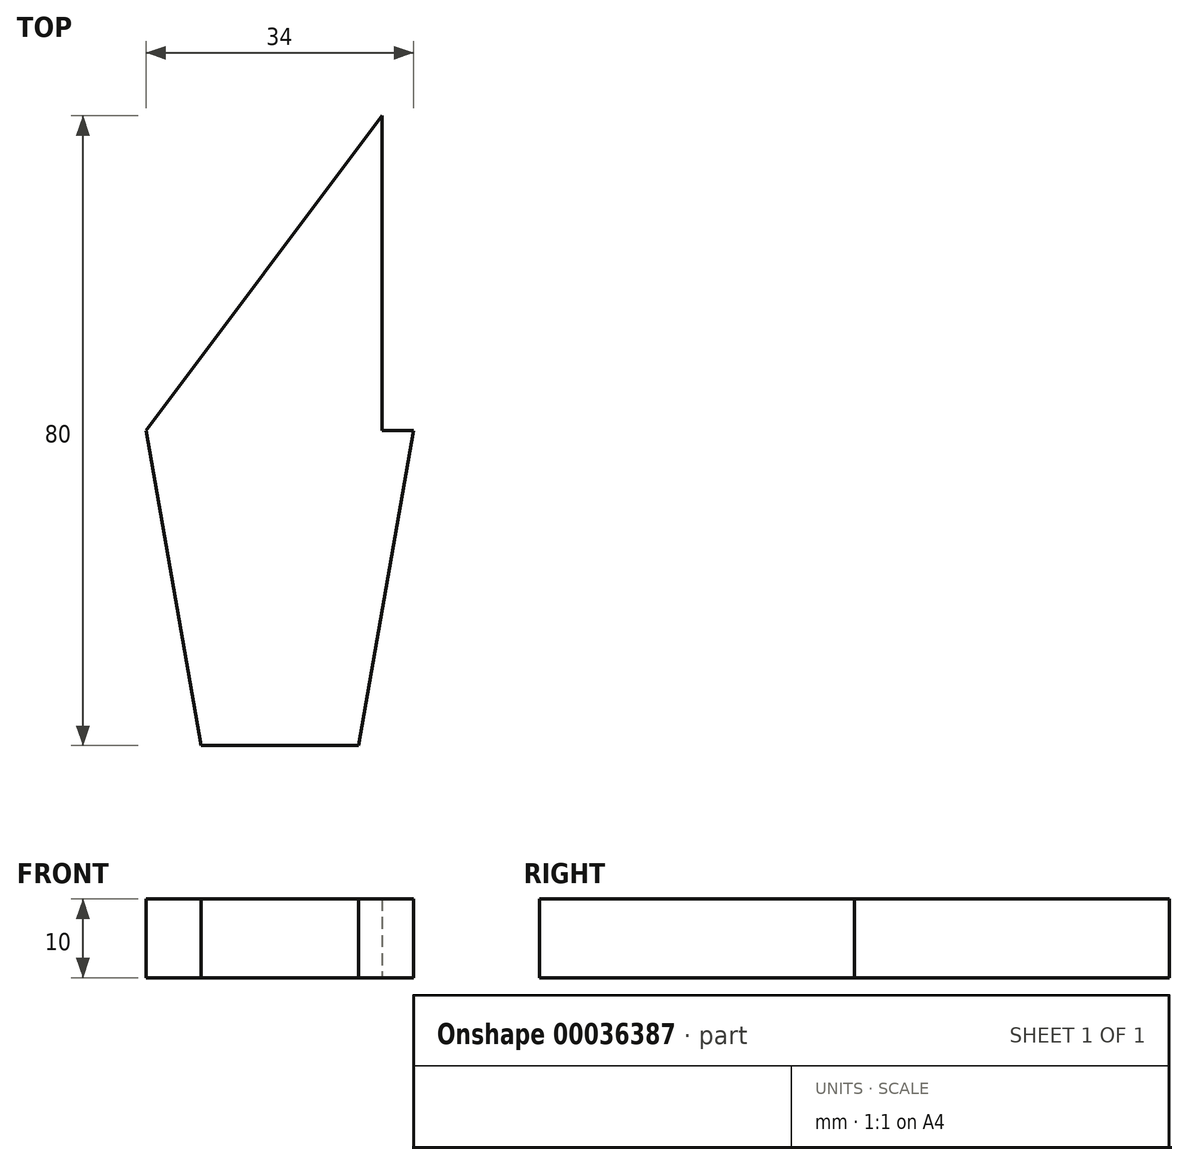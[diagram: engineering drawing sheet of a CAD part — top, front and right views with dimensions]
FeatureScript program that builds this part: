
annotation { "Feature Type Name" : "Feature", "Feature Type Description" : "" }
export const myFeature = defineFeature(function(context is Context, id is Id, definition is map)
    precondition{}
    {
        {
            var Q0;
            Q0=qCreatedBy(makeId("Top.planeOp"),FACE);
            var sketch = newSketch(context, id + "F0", { "sketchPlane" : qUnion([Q0])});
            skLineSegment(sketch, "E0.bottom", {"start": v(-54.45, 18.14) * mm, "end": v(-20.45, 18.14) * mm});
            skLineSegment(sketch, "E0.top", {"start": v(-47.45, -21.86) * mm, "end": v(-27.45, -21.86) * mm});
            skLineSegment(sketch, "E1", {"start": v(-54.45, 18.14) * mm, "end": v(-47.45, -21.86) * mm});
            skLineSegment(sketch, "E2", {"start": v(-20.45, 18.14) * mm, "end": v(-27.45, -21.86) * mm});
            skLineSegment(sketch, "E3", {"start": v(-24.45, 18.14) * mm, "end": v(-24.45, 58.14) * mm});
            skLineSegment(sketch, "E4", {"start": v(-24.45, 58.14) * mm, "end": v(-54.45, 18.14) * mm});
            skSolve(sketch);
        }
        {
            var Q0;
            Q0=makeQuery(id+"F0.imprint","IMPRINT",FACE,{"disambiguationData":[TD([[makeQuery(id+"F0.imprint","IMPRINT",EDGE,{"derivedFrom":sQuery(id+"F0.wireOp",EDGE,"E0.top")}),1.0]])]});
            var Q1;
            {var subQ1=sQuery(id+"F0.wireOp",EDGE,"E3");Q1=makeQuery(id+"F0.imprint","IMPRINT",FACE,{"disambiguationData":[TD([[makeQuery(id+"F0.imprint","IMPRINT",EDGE,{"derivedFrom":subQ1}),1.0]])]});}
            extrude(context, id + "F1", {"entities" : qUnion([Q0, Q1]), "depth" : 10 * mm});
        }
    });
